# Revit family: FP_Revit_18_HCB30-6_N_Rangehood_90001233A
name_source: partatom
category: Specialty Equipment
revit_build: Autodesk Revit 2018 (Build: 20170223_1515(x64)
units: mm (PartAtom-declared; Revit-internal decimal feet)

## family parameters
Always vertical = Yes
Cut with Voids When Loaded = Yes
OmniClass Number = 23.40.40.00
OmniClass Title = Food Service Equipment and Furnishings
Part Type = Normal
Room Calculation Point = No
Round Connector Dimension = Use Diameter
Shared = No
Work Plane-Based = No

## types (1)
- FP_Revit_18_HCB30-6_N_Rangehood_90001233A
    Connector Description - Electrical = 120 V, 60 Hz, 20 A, Branch circuit
    Connector Description - Extraction = 8" (208mm) Outside diameter of ducting outlet, 600 CFM
    Description = 30" Professional Rangehood
    Manufacturer = Fisher & Paykel Appliances
    Material - Body = Fisher & Paykel - Stainless Steel
    Material - Buttons and Dials = Fisher & Paykel - Steel, Chrome Plated
    Material - Glass = Fisher & Paykel - White Bezel
    Model = HCB30-6_N
    Product - Depth = 636 mm  [stored 2.08661 ft]
    Product - Height = 457 mm  [stored 1.49934 ft]
    Product - Width = 759 mm
    URL = www.fisherpaykel.com

note: [stored X ft] marks values corroborated as IEEE doubles in the binary element streams (Revit-internal decimal feet)

## geometry (parser evidence)
native form markers: Sweep x5
no freeform markers — native parametric forms only
